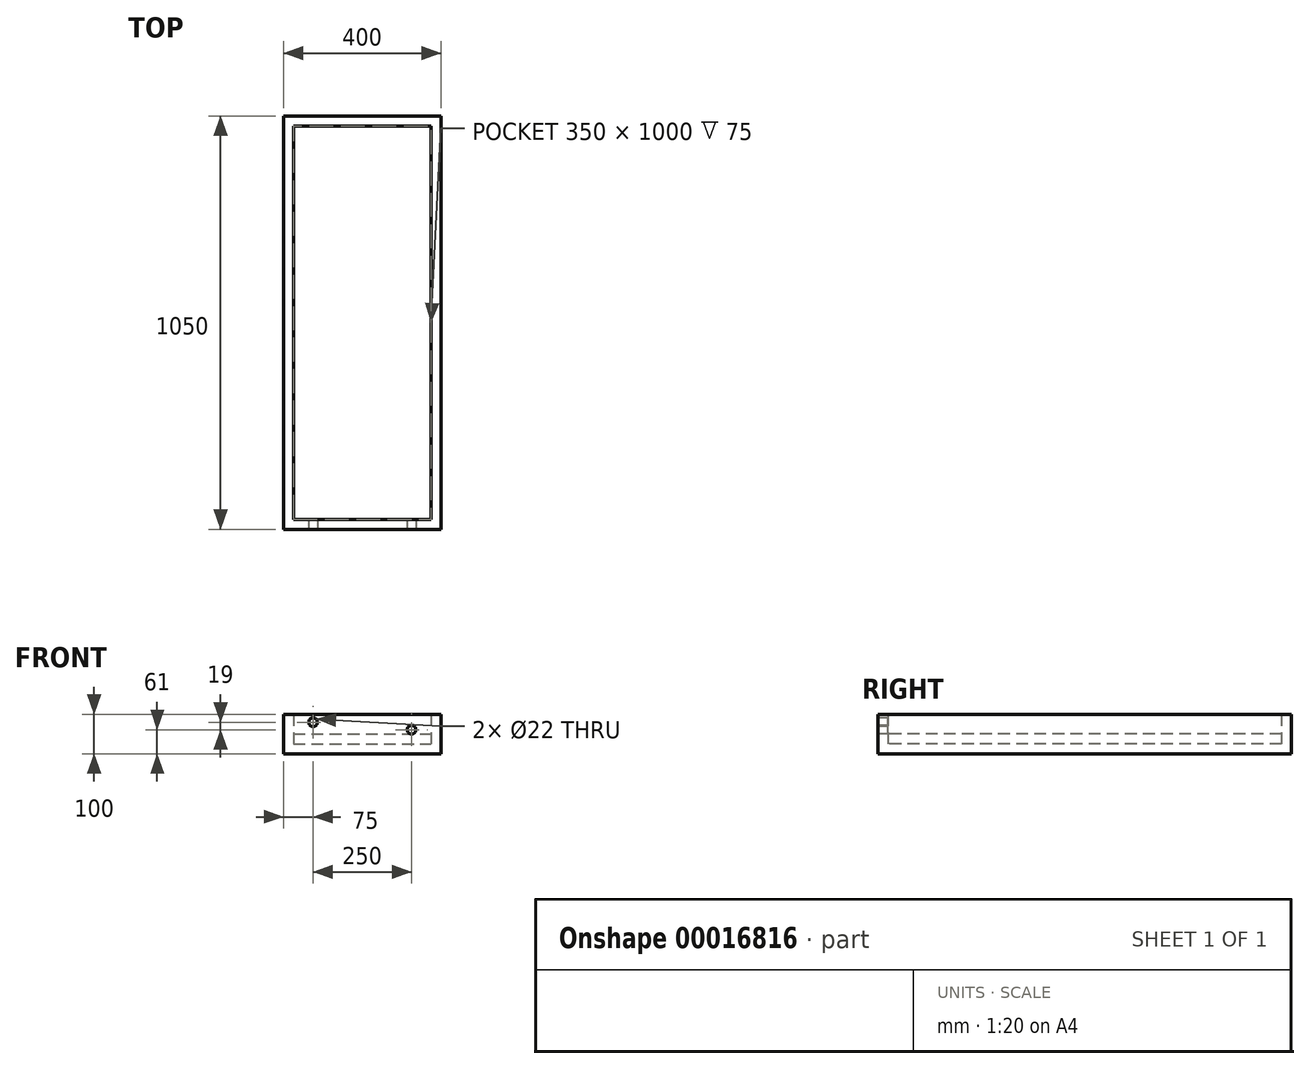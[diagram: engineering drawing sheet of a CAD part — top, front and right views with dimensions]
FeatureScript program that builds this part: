
annotation { "Feature Type Name" : "Feature", "Feature Type Description" : "" }
export const myFeature = defineFeature(function(context is Context, id is Id, definition is map)
    precondition{}
    {
        {
            var Q0;
            Q0=qCreatedBy(makeId("Top.planeOp"),FACE);
            var sketch = newSketch(context, id + "F0", { "sketchPlane" : qUnion([Q0])});
            skLineSegment(sketch, "E0.bottom", {"start": v(0, 0) * mm, "end": v(400, 0) * mm});
            skLineSegment(sketch, "E0.top", {"start": v(0, -1050) * mm, "end": v(400, -1050) * mm});
            skLineSegment(sketch, "E0.left", {"start": v(0, 0) * mm, "end": v(0, -1050) * mm});
            skLineSegment(sketch, "E0.right", {"start": v(400, 0) * mm, "end": v(400, -1050) * mm});
            skSolve(sketch);
        }
        {
            var Q0;
            Q0 = qSketchRegion(id + "F0", true);
            extrude(context, id + "F1", {"entities" : qUnion([Q0]), "depth" : 25 * mm});
        }
        {
            var Q0;
            Q0=makeQuery(id+"F1.opExtrude","CAP_FACE",FACE,{"disambiguationData":[OSD([sQuery(id+"F0.wireOp",EDGE,"E0.bottom"),sQuery(id+"F0.wireOp",EDGE,"E0.top"),sQuery(id+"F0.wireOp",EDGE,"E0.left"),sQuery(id+"F0.wireOp",EDGE,"E0.right")])],"isStart":false});
            var sketch = newSketch(context, id + "F2", { "sketchPlane" : qUnion([Q0])});
            skLineSegment(sketch, "E1", {"start": v(0, -1050) * mm, "end": v(400, -1050) * mm});
            skLineSegment(sketch, "E2", {"start": v(400, -1050) * mm, "end": v(400, 0) * mm});
            skLineSegment(sketch, "E3", {"start": v(400, 0) * mm, "end": v(0, 0) * mm});
            skLineSegment(sketch, "E4", {"start": v(0, 0) * mm, "end": v(0, -1050) * mm});
            skLineSegment(sketch, "E5", {"start": v(25, -1025) * mm, "end": v(375, -1025) * mm});
            skLineSegment(sketch, "E6", {"start": v(375, -1025) * mm, "end": v(375, -25) * mm});
            skLineSegment(sketch, "E7", {"start": v(375, -25) * mm, "end": v(25, -25) * mm});
            skLineSegment(sketch, "E8", {"start": v(25, -25) * mm, "end": v(25, -1025) * mm});
            skSolve(sketch);
        }
        {
            var Q0;
            Q0 = qSketchRegion(id + "F2", true);
            extrude(context, id + "F3", {"entities" : qUnion([Q0]), "operationType" : NewBodyOperationType.ADD, "depth" : 75 * mm});
        }
        {
            var Q0;
            Q0=makeQuery(id+"F3.boolean.opBoolean","MERGE",FACE,{"derivedFrom":[makeQuery(id+"F1.opExtrude","SWEPT_FACE",FACE,{"disambiguationData":[OSD([sQuery(id+"F0.wireOp",EDGE,"E0.top")])]}),makeQuery(id+"F3.opExtrude","SWEPT_FACE",FACE,{"disambiguationData":[OSD([sQuery(id+"F2.wireOp",EDGE,"E1")])]})]});
            var sketch = newSketch(context, id + "F4", { "sketchPlane" : qUnion([Q0])});
            skCircle(sketch, "E9", {"center": v(75, 80) * mm, "radius": 11 * mm});
            skCircle(sketch, "E10", {"center": v(325, 61) * mm, "radius": 11 * mm});
            skSolve(sketch);
        }
        {
            var Q0;
            Q0=makeQuery(id+"F4.imprint","IMPRINT",FACE,{"disambiguationData":[TD([[makeQuery(id+"F4.imprint","IMPRINT",EDGE,{"derivedFrom":sQuery(id+"F4.wireOp",EDGE,"E10")}),1.0]])]});
            var Q1;
            Q1=makeQuery(id+"F4.imprint","IMPRINT",FACE,{"disambiguationData":[TD([[makeQuery(id+"F4.imprint","IMPRINT",EDGE,{"derivedFrom":sQuery(id+"F4.wireOp",EDGE,"E9")}),1.0]])]});
            extrude(context, id + "F5", {"entities" : qUnion([Q0, Q1]), "operationType" : NewBodyOperationType.REMOVE, "oppositeDirection" : true, "depth" : 25 * mm});
        }
        {
            var Q0;
            Q0=makeQuery(id+"F1.opExtrude","CAP_FACE",FACE,{"disambiguationData":[OSD([sQuery(id+"F0.wireOp",EDGE,"E0.bottom"),sQuery(id+"F0.wireOp",EDGE,"E0.top"),sQuery(id+"F0.wireOp",EDGE,"E0.left"),sQuery(id+"F0.wireOp",EDGE,"E0.right")])],"isStart":false});
            extrude(context, id + "F6", {"entities" : qUnion([Q0]), "depth" : 25 * mm});
        }
    });
